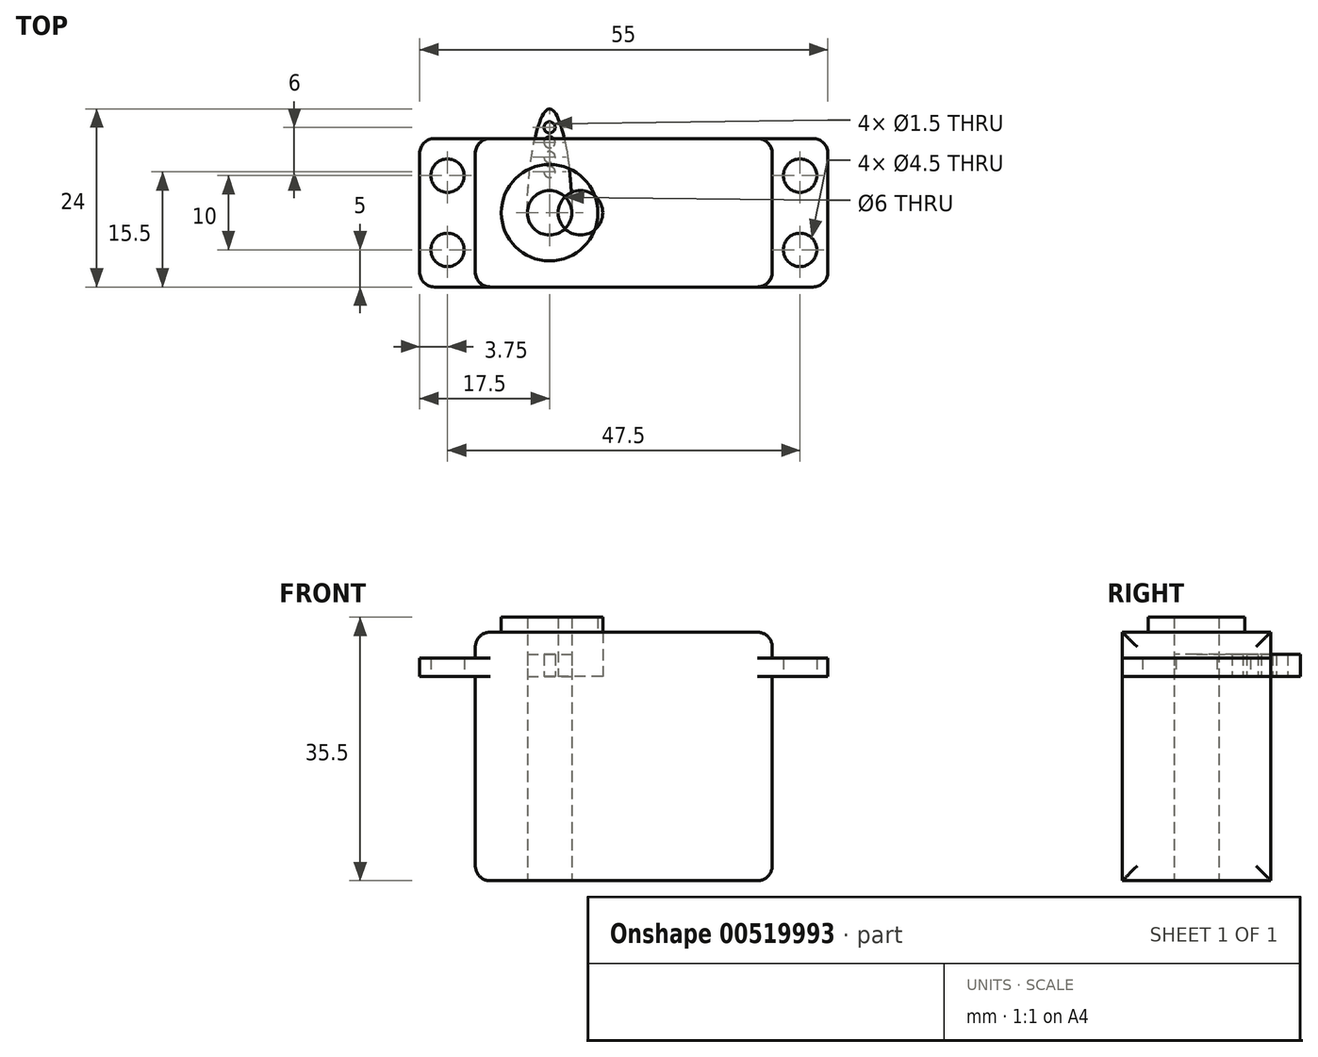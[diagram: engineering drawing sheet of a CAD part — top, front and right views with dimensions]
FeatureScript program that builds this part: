
annotation { "Feature Type Name" : "Feature", "Feature Type Description" : "" }
export const myFeature = defineFeature(function(context is Context, id is Id, definition is map)
    precondition{}
    {
        {
            var Q0;
            Q0=qCreatedBy(makeId("Top.planeOp"),FACE);
            var sketch = newSketch(context, id + "F0", { "sketchPlane" : qUnion([Q0])});
            skLineSegment(sketch, "E0.bottom", {"start": v(20, -10) * mm, "end": v(-20, -10) * mm});
            skLineSegment(sketch, "E0.top", {"start": v(20, 10) * mm, "end": v(-20, 10) * mm});
            skLineSegment(sketch, "E0.left", {"start": v(20, -10) * mm, "end": v(20, 10) * mm});
            skLineSegment(sketch, "E0.right", {"start": v(-20, -10) * mm, "end": v(-20, 10) * mm});
            skPoint(sketch, "E0.middle", {"position": v(0, 0) * mm});
            skLineSegment(sketch, "E1.bottom", {"start": v(27.5, -10) * mm, "end": v(-27.5, -10) * mm});
            skLineSegment(sketch, "E1.top", {"start": v(27.5, 10) * mm, "end": v(-27.5, 10) * mm});
            skLineSegment(sketch, "E1.left", {"start": v(27.5, -10) * mm, "end": v(27.5, 10) * mm});
            skLineSegment(sketch, "E1.right", {"start": v(-27.5, -10) * mm, "end": v(-27.5, 10) * mm});
            skCircle(sketch, "E2", {"center": v(-23.75, 5) * mm, "radius": 2.25 * mm});
            skCircle(sketch, "E3", {"center": v(-23.75, -5) * mm, "radius": 2.25 * mm});
            skCircle(sketch, "E4", {"center": v(23.75, 5) * mm, "radius": 2.25 * mm});
            skCircle(sketch, "E5", {"center": v(23.75, -5) * mm, "radius": 2.25 * mm});
            skCircle(sketch, "E6", {"center": v(-10, 0) * mm, "radius": 6.5 * mm});
            skCircle(sketch, "E7", {"center": v(-10, 0) * mm, "radius": 3 * mm});
            skSolve(sketch);
        }
        {
            var Q0;
            {var subQ2=sQuery(id+"F0.wireOp",EDGE,"E0.left");Q0=makeQuery(id+"F0.imprint","IMPRINT",FACE,{"disambiguationData":[TD([[makeQuery(id+"F0.imprint","IMPRINT",EDGE,{"derivedFrom":subQ2}),-1.0]])]});}
            var Q1;
            {var subQ1=sQuery(id+"F0.wireOp",EDGE,"E0.right");Q1=makeQuery(id+"F0.imprint","IMPRINT",FACE,{"disambiguationData":[TD([[makeQuery(id+"F0.imprint","IMPRINT",EDGE,{"derivedFrom":subQ1}),1.0]])]});}
            extrude(context, id + "F1", {"entities" : qUnion([Q0, Q1]), "depth" : 2.5 * mm, "offsetDistance" : 25 * mm});
        }
        {
            var Q0;
            {var subQ1=sQuery(id+"F0.wireOp",EDGE,"E0.left");Q0=makeQuery(id+"F0.imprint","IMPRINT",FACE,{"disambiguationData":[TD([[makeQuery(id+"F0.imprint","IMPRINT",EDGE,{"derivedFrom":subQ1}),1.0]])]});}
            extrude(context, id + "F2", {"entities" : qUnion([Q0]), "depth" : 6 * mm, "offsetDistance" : 25 * mm});
        }
        {
            var Q0;
            {var subQ1=sQuery(id+"F0.wireOp",EDGE,"E0.left");Q0=makeQuery(id+"F0.imprint","IMPRINT",FACE,{"disambiguationData":[TD([[makeQuery(id+"F0.imprint","IMPRINT",EDGE,{"derivedFrom":subQ1}),1.0]])]});}
            extrude(context, id + "F3", {"entities" : qUnion([Q0]), "operationType" : NewBodyOperationType.ADD, "depth" : -27.5 * mm, "offsetDistance" : 25 * mm});
        }
        {
            var Q0;
            Q0=makeQuery(id+"F0.imprint","IMPRINT",FACE,{"disambiguationData":[TD([[makeQuery(id+"F0.imprint","IMPRINT",EDGE,{"derivedFrom":sQuery(id+"F0.wireOp",EDGE,"E6")}),1.0]])]});
            extrude(context, id + "F4", {"entities" : qUnion([Q0]), "operationType" : NewBodyOperationType.ADD, "depth" : 8 * mm, "offsetDistance" : 25 * mm});
        }
        {
            var Q0;
            Q0=makeQuery(id+"F1.opExtrude","SWEPT_EDGE",EDGE,{"disambiguationData":[OSD([sQuery(id+"F0.wireOp",EDGE,"E1.bottom"),sQuery(id+"F0.wireOp",EDGE,"E1.right")])]});
            var Q1;
            Q1=makeQuery(id+"F1.opExtrude","SWEPT_EDGE",EDGE,{"disambiguationData":[OSD([sQuery(id+"F0.wireOp",EDGE,"E1.bottom"),sQuery(id+"F0.wireOp",EDGE,"E1.left")])]});
            var Q2;
            Q2=makeQuery(id+"F1.opExtrude","SWEPT_EDGE",EDGE,{"disambiguationData":[OSD([sQuery(id+"F0.wireOp",EDGE,"E1.top"),sQuery(id+"F0.wireOp",EDGE,"E1.left")])]});
            var Q3;
            Q3=makeQuery(id+"F1.opExtrude","SWEPT_EDGE",EDGE,{"disambiguationData":[OSD([sQuery(id+"F0.wireOp",EDGE,"E1.top"),sQuery(id+"F0.wireOp",EDGE,"E1.right")])]});
            var Q4;
            Q4=makeQuery(id+"F2.opExtrude","CAP_EDGE",EDGE,{"disambiguationData":[OSD([sQuery(id+"F0.wireOp",EDGE,"E1.bottom")])],"isStart":false});
            var Q5;
            Q5=makeQuery(id+"F2.opExtrude","CAP_EDGE",EDGE,{"disambiguationData":[OSD([sQuery(id+"F0.wireOp",EDGE,"E1.top")])],"isStart":false});
            var Q6;
            Q6=makeQuery(id+"F3.opExtrude","CAP_EDGE",EDGE,{"disambiguationData":[OSD([sQuery(id+"F0.wireOp",EDGE,"E1.top")])],"isStart":false});
            var Q7;
            Q7=makeQuery(id+"F3.opExtrude","CAP_EDGE",EDGE,{"disambiguationData":[OSD([sQuery(id+"F0.wireOp",EDGE,"E1.bottom")])],"isStart":false});
            var Q8;
            {var subQ0=sQuery(id+"F0.wireOp",EDGE,"E1.top");var subQ1=sQuery(id+"F0.wireOp",EDGE,"E0.right");Q8=makeQuery(id+"F3.boolean.opBoolean","MERGE",EDGE,{"derivedFrom":[makeQuery(id+"F2.opExtrude","SWEPT_EDGE",EDGE,{"disambiguationData":[OSD([subQ1,subQ0])]}),makeQuery(id+"F3.opExtrude","SWEPT_EDGE",EDGE,{"disambiguationData":[OSD([subQ1,subQ0])]})]});}
            var Q9;
            {var subQ0=sQuery(id+"F0.wireOp",EDGE,"E1.bottom");var subQ1=sQuery(id+"F0.wireOp",EDGE,"E0.right");Q9=makeQuery(id+"F3.boolean.opBoolean","MERGE",EDGE,{"derivedFrom":[makeQuery(id+"F2.opExtrude","SWEPT_EDGE",EDGE,{"disambiguationData":[OSD([subQ1,subQ0])]}),makeQuery(id+"F3.opExtrude","SWEPT_EDGE",EDGE,{"disambiguationData":[OSD([subQ1,subQ0])]})]});}
            var Q10;
            {var subQ0=sQuery(id+"F0.wireOp",EDGE,"E1.bottom");var subQ1=sQuery(id+"F0.wireOp",EDGE,"E0.left");Q10=makeQuery(id+"F3.boolean.opBoolean","MERGE",EDGE,{"derivedFrom":[makeQuery(id+"F2.opExtrude","SWEPT_EDGE",EDGE,{"disambiguationData":[OSD([subQ1,subQ0])]}),makeQuery(id+"F3.opExtrude","SWEPT_EDGE",EDGE,{"disambiguationData":[OSD([subQ1,subQ0])]})]});}
            var Q11;
            {var subQ0=sQuery(id+"F0.wireOp",EDGE,"E1.top");var subQ1=sQuery(id+"F0.wireOp",EDGE,"E0.left");Q11=makeQuery(id+"F3.boolean.opBoolean","MERGE",EDGE,{"derivedFrom":[makeQuery(id+"F2.opExtrude","SWEPT_EDGE",EDGE,{"disambiguationData":[OSD([subQ1,subQ0])]}),makeQuery(id+"F3.opExtrude","SWEPT_EDGE",EDGE,{"disambiguationData":[OSD([subQ1,subQ0])]})]});}
            var Q12;
            Q12=makeQuery(id+"F3.opExtrude","CAP_EDGE",EDGE,{"disambiguationData":[OSD([sQuery(id+"F0.wireOp",EDGE,"E0.left")])],"isStart":false});
            var Q13;
            Q13=makeQuery(id+"F2.opExtrude","CAP_EDGE",EDGE,{"disambiguationData":[OSD([sQuery(id+"F0.wireOp",EDGE,"E0.left")])],"isStart":false});
            var Q14;
            Q14=makeQuery(id+"F2.opExtrude","CAP_EDGE",EDGE,{"disambiguationData":[OSD([sQuery(id+"F0.wireOp",EDGE,"E0.right")])],"isStart":false});
            var Q15;
            Q15=makeQuery(id+"F3.opExtrude","CAP_EDGE",EDGE,{"disambiguationData":[OSD([sQuery(id+"F0.wireOp",EDGE,"E0.right")])],"isStart":false});
            fillet(context, id + "F5", {"entities" : qUnion([Q0, Q1, Q2, Q3, Q4, Q5, Q6, Q7, Q8, Q9, Q10, Q11, Q12, Q13, Q14, Q15]), "radius" : 2 * mm, "tangentPropagation" : true, "allowEdgeOverflow" : false});
        }
        {
            var Q0;
            {var subQ0=sQuery(id+"F0.wireOp",EDGE,"E7");Q0=makeQuery(id+"FQHcsVbczDKKGZd_3.boolean.opBoolean","MERGE",FACE,{"derivedFrom":[makeQuery(id+"F4.opExtrude","CAP_FACE",FACE,{"disambiguationData":[OSD([sQuery(id+"F0.wireOp",EDGE,"E6"),subQ0])],"isStart":true}),makeQuery(id+"FQHcsVbczDKKGZd_3.opExtrude","CAP_FACE",FACE,{"disambiguationData":[OSD([subQ0])],"isStart":true})]});}
            extrude(context, id + "F6", {"entities" : qUnion([Q0]), "operationType" : NewBodyOperationType.ADD, "depth" : 27.5 * mm, "offsetDistance" : 25 * mm});
        }
        {
            var Q0;
            Q0=qCreatedBy(makeId("Top.planeOp"),FACE);
            var sketch = newSketch(context, id + "F7", { "sketchPlane" : qUnion([Q0])});
            skCircle(sketch, "E8", {"center": v(-10, 0) * mm, "radius": 3 * mm});
            skFitSpline(sketch, "E9", {"points": [v(-13, 0) * mm, v(-10, 14) * mm, v(-7, 0) * mm], "startDerivative": vector(0, 42) * mm, "endDerivative": vector(0, -42) * mm});
            skCircle(sketch, "E10", {"center": v(-10, 7.5) * mm, "radius": 0.75 * mm});
            skCircle(sketch, "E11", {"center": v(-10, 9.5) * mm, "radius": 0.75 * mm});
            skCircle(sketch, "E12", {"center": v(-10, 5.5) * mm, "radius": 0.75 * mm});
            skCircle(sketch, "E13", {"center": v(-10, 11.5) * mm, "radius": 0.75 * mm});
            skSolve(sketch);
        }
        {
            var Q0;
            Q0 = qSketchRegion(id + "F7", true);
            extrude(context, id + "F8", {"entities" : qUnion([Q0]), "depth" : 3 * mm, "offsetDistance" : 25 * mm});
        }
        {
            var Q0;
            Q0=makeQuery(id+"F7.imprint","IMPRINT",FACE,{"disambiguationData":[TD([[makeQuery(id+"F7.imprint","IMPRINT",EDGE,{"derivedFrom":sQuery(id+"F7.wireOp",EDGE,"E8")}),1.0]])]});
            var Q1;
            {var subQ0=sQuery(id+"F7.wireOp",EDGE,"E9");Q1=makeQuery(id+"F7.imprint","IMPRINT",FACE,{"disambiguationData":[TD([[makeQuery(id+"F7.imprint","IMPRINT",EDGE,{"derivedFrom":subQ0}),-1.0]])]});}
            extrude(context, id + "F9", {"entities" : qUnion([Q0, Q1]), "depth" : 3 * mm, "offsetDistance" : 25 * mm});
        }
        {
            var Q0;
            Q0=makeQuery(id+"F9.opExtrude","SWEPT_BODY",BODY,{"disambiguationData":[OSD([sQuery(id+"F7.wireOp",EDGE,"E8"),sQuery(id+"F7.wireOp",EDGE,"E9"),sQuery(id+"F7.wireOp",EDGE,"E10"),sQuery(id+"F7.wireOp",EDGE,"E11"),sQuery(id+"F7.wireOp",EDGE,"E12"),sQuery(id+"F7.wireOp",EDGE,"E13")])]});
            deleteBodies(context, id + "F10", {"entities" : qUnion([Q0])});
        }
        {
            var Q0;
            Q0=qCreatedBy(makeId("Top.planeOp"),FACE);
            var sketch = newSketch(context, id + "F11", { "sketchPlane" : qUnion([Q0])});
            skCircle(sketch, "E14", {"center": v(-5.84, 0) * mm, "radius": 3 * mm});
            skSolve(sketch);
        }
        {
            var Q0;
            Q0=makeQuery(id+"F11.imprint","IMPRINT",FACE,{"disambiguationData":[TD([[makeQuery(id+"F11.imprint","IMPRINT",EDGE,{"derivedFrom":sQuery(id+"F11.wireOp",EDGE,"E14")}),1.0]])]});
            extrude(context, id + "F12", {"entities" : qUnion([Q0]), "depth" : 8 * mm, "offsetDistance" : 25 * mm});
        }
    });
